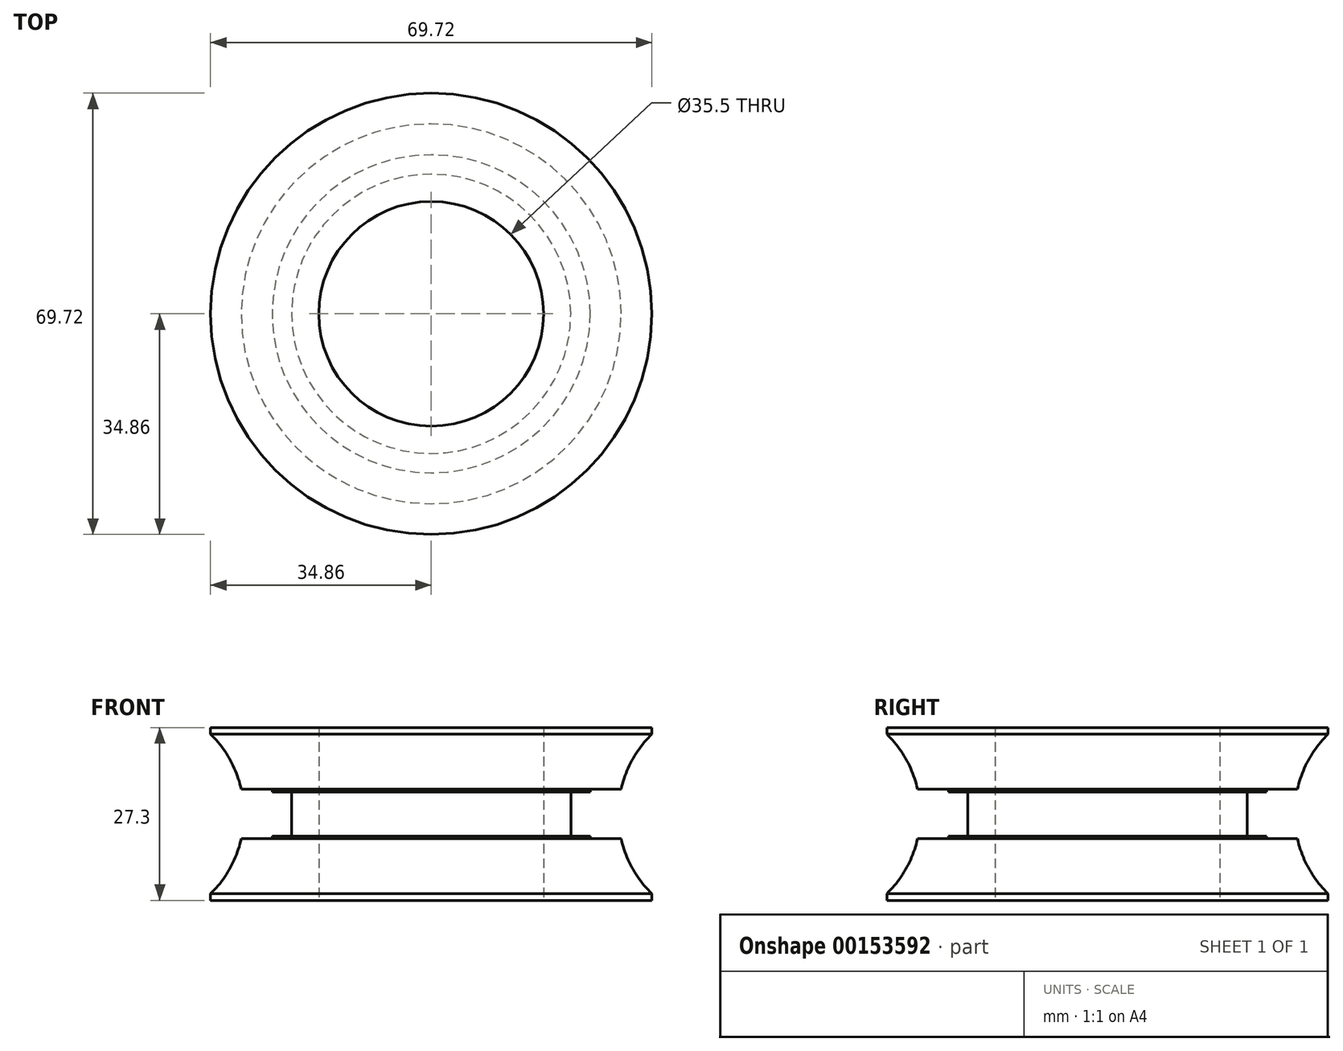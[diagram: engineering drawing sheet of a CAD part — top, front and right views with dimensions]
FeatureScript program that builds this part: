
annotation { "Feature Type Name" : "Feature", "Feature Type Description" : "" }
export const myFeature = defineFeature(function(context is Context, id is Id, definition is map)
    precondition{}
    {
        {
            var Q0;
            Q0=qCreatedBy(makeId("Front.planeOp"),FACE);
            var sketch = newSketch(context, id + "F0", { "sketchPlane" : qUnion([Q0])});
            skLineSegment(sketch, "E0", {"start": v(0, 0) * mm, "end": v(0, 28) * mm, "construction": true});
            skLineSegment(sketch, "E1", {"start": v(-17.75, 0) * mm, "end": v(-17.75, 13.65) * mm});
            skLineSegment(sketch, "E2", {"start": v(-36, 0) * mm, "end": v(-36, 28) * mm, "construction": true});
            skLineSegment(sketch, "E3", {"start": v(-30, 28) * mm, "end": v(-30, 0) * mm, "construction": true});
            skLineSegment(sketch, "E4", {"start": v(-22.05, 10.15) * mm, "end": v(-22.05, 17.15) * mm});
            skPoint(sketch, "E5", {"position": v(-22.05, 10.15) * mm});
            skLineSegment(sketch, "E6", {"start": v(-17.75, 0) * mm, "end": v(-36, 0) * mm});
            skLineSegment(sketch, "E7", {"start": v(-25.12, 17.55) * mm, "end": v(-25.12, 17.15) * mm});
            skPoint(sketch, "E8", {"position": v(-22.05, 17.15) * mm});
            skPoint(sketch, "E9.orphan", {"position": v(-22.05, 28) * mm});
            skPoint(sketch, "E10.orphan", {"position": v(-22.05, 0) * mm});
            skPoint(sketch, "E11", {"position": v(-25.12, 9.75) * mm});
            skPoint(sketch, "E12", {"position": v(-22.05, 13.65) * mm});
            skLineSegment(sketch, "E13", {"start": v(-22.05, 10.15) * mm, "end": v(-25.12, 10.15) * mm});
            skLineSegment(sketch, "E14", {"start": v(-25.12, 9.75) * mm, "end": v(-30, 9.75) * mm});
            skLineSegment(sketch, "E15", {"start": v(-36, 13.65) * mm, "end": v(0, 13.65) * mm, "construction": true});
            skLineSegment(sketch, "E16.MirrorCS", {"start": v(-22.05, 17.15) * mm, "end": v(-25.12, 17.15) * mm});
            skLineSegment(sketch, "E17.MirrorCS", {"start": v(-25.12, 17.55) * mm, "end": v(-30, 17.55) * mm});
            skPoint(sketch, "E18.start.orphan", {"position": v(-17.75, 28) * mm});
            skLineSegment(sketch, "E19.MirrorCS", {"start": v(-17.75, 27.3) * mm, "end": v(-36, 27.3) * mm});
            skLineSegment(sketch, "E20.MirrorCS", {"start": v(-17.75, 27.3) * mm, "end": v(-17.75, 13.65) * mm});
            skLineSegment(sketch, "E21.MirrorCS", {"start": v(-25.12, 9.75) * mm, "end": v(-25.12, 10.15) * mm});
            skArc(sketch, "E22", {"start": v(-36, 0) * mm, "mid": v(-32.19, 4.38) * mm, "end": v(-30, 9.75) * mm});
            skArc(sketch, "E23.trimOffspring", {"start": v(-30, 17.55) * mm, "mid": v(-32.19, 22.92) * mm, "end": v(-36, 27.3) * mm});
            skLineSegment(sketch, "E24.trimOffspring", {"start": v(-25.12, 10.15) * mm, "end": v(-25.12, 0) * mm});
            skLineSegment(sketch, "E25.trimOffspring", {"start": v(-25.12, 17.15) * mm, "end": v(-25.12, 27.3) * mm});
            skSolve(sketch);
        }
        {
            var Q0;
            Q0=qSketchRegion(id+"F0",true);
            var Q1;
            Q1=sQuery(id+"F0.wireOp",EDGE,"E0");
            revolve(context, id + "F1", {"entities" : qUnion([Q0]), "axis" : qUnion([Q1]), "revolveType" : RevolveType.FULL});
        }
        {
            var Q0;
            Q0=makeQuery(id+"F1.opRevolve","SWEPT_EDGE",EDGE,{"disambiguationData":[OSD([sQuery(id+"F0.wireOp",EDGE,"E19.MirrorCS"),sQuery(id+"F0.wireOp",EDGE,"E23.trimOffspring")])]});
            chamfer(context, id + "F2", {"entities" : qUnion([Q0]), "chamferType" : ChamferType.OFFSET_ANGLE, "width" : 1.25 * mm, "oppositeDirection" : true, "angle" : 90 * degree, "tangentPropagation" : true});
        }
        {
            var Q0;
            Q0=makeQuery(id+"F1.opRevolve","SWEPT_EDGE",EDGE,{"disambiguationData":[OSD([sQuery(id+"F0.wireOp",EDGE,"E6"),sQuery(id+"F0.wireOp",EDGE,"E22")])]});
            chamfer(context, id + "F3", {"entities" : qUnion([Q0]), "chamferType" : ChamferType.OFFSET_ANGLE, "width" : 1.25 * mm, "oppositeDirection" : false, "angle" : 90 * degree, "tangentPropagation" : true});
        }
    });
